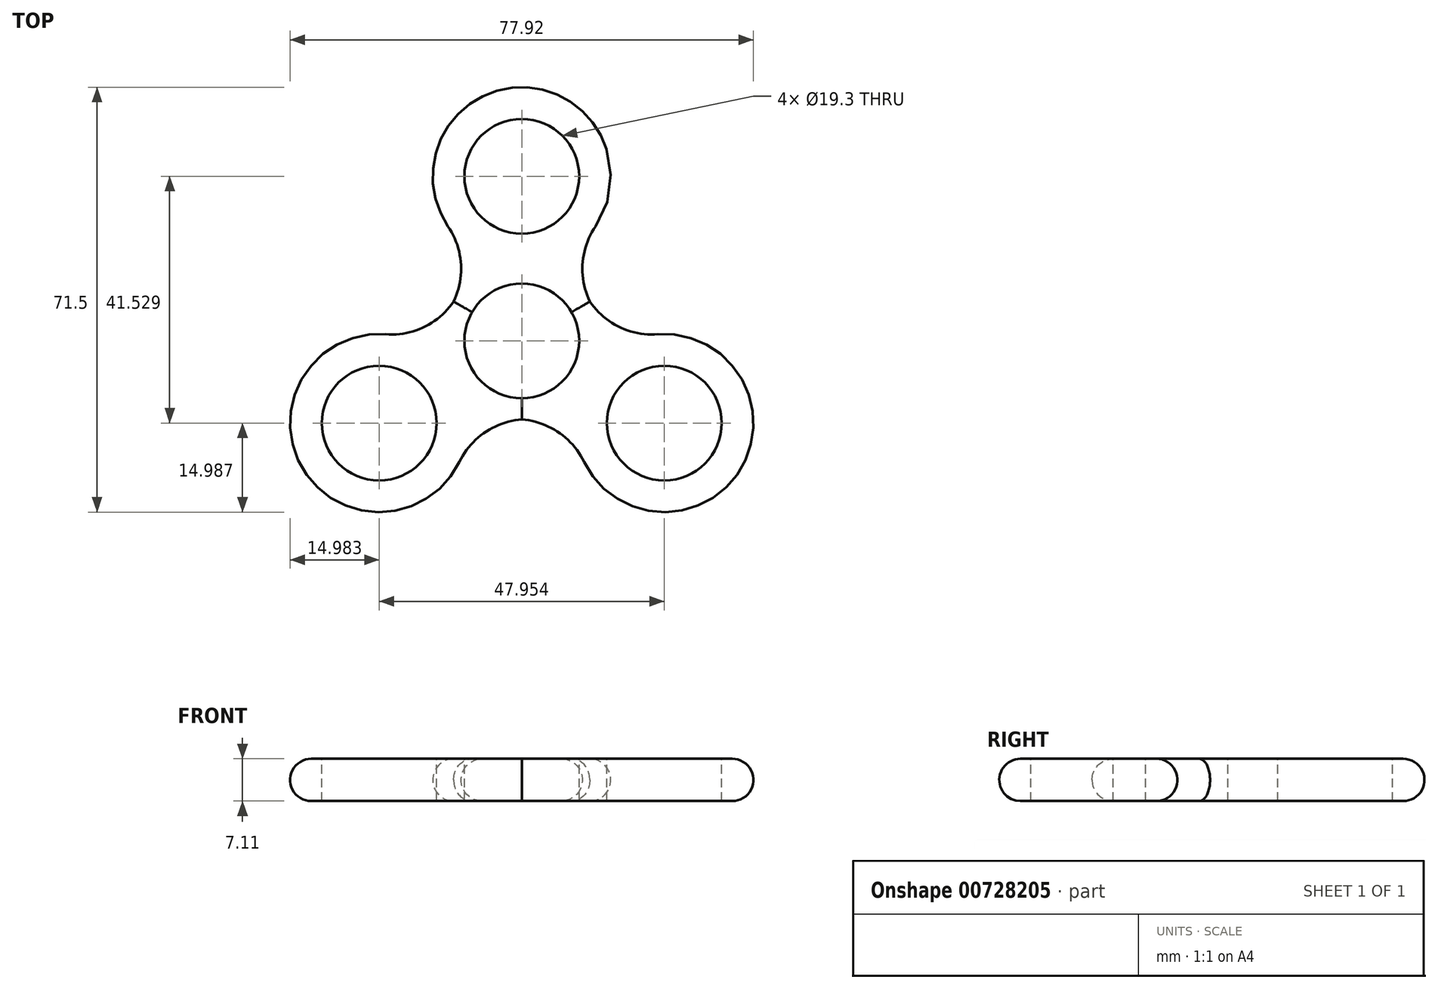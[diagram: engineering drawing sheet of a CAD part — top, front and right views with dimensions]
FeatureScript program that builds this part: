
annotation { "Feature Type Name" : "Feature", "Feature Type Description" : "" }
export const myFeature = defineFeature(function(context is Context, id is Id, definition is map)
    precondition{}
    {
        {
            var Q0;
            Q0=qCreatedBy(makeId("Top.planeOp"),FACE);
            var sketch = newSketch(context, id + "F0", { "sketchPlane" : qUnion([Q0])});
            skArc(sketch, "E0", {"start": v(12.4, 19.26) * mm, "mid": v(0, 42.67) * mm, "end": v(-12.4, 19.26) * mm});
            skArc(sketch, "E1.1.0", {"start": v(-22.88, 1.1) * mm, "mid": v(-36.96, -21.34) * mm, "end": v(-10.48, -20.36) * mm});
            skArc(sketch, "E1.2.0", {"start": v(10.48, -20.36) * mm, "mid": v(36.96, -21.34) * mm, "end": v(22.88, 1.1) * mm});
            skPoint(sketch, "E1.center", {"position": v(0, 0) * mm});
            skPoint(sketch, "E2.visualSharp", {"position": v(-12.53, -4.17) * mm});
            skArc(sketch, "E2.filletArc", {"start": v(-22.88, 1.1) * mm, "mid": v(-16.21, 2.44) * mm, "end": v(-11.19, 7.02) * mm});
            skPoint(sketch, "E3.visualSharp", {"position": v(12.53, -4.17) * mm});
            skArc(sketch, "E3.filletArc", {"start": v(11.19, 7.02) * mm, "mid": v(16.21, 2.44) * mm, "end": v(22.88, 1.1) * mm});
            skPoint(sketch, "E4.visualSharp", {"position": v(2.66, 12.94) * mm});
            skArc(sketch, "E4.filletArc", {"start": v(12.4, 19.26) * mm, "mid": v(10.22, 12.82) * mm, "end": v(11.67, 6.18) * mm});
            skPoint(sketch, "E5.visualSharp", {"position": v(-2.66, 12.94) * mm});
            skArc(sketch, "E5.filletArc", {"start": v(-11.67, 6.18) * mm, "mid": v(-10.22, 12.82) * mm, "end": v(-12.4, 19.26) * mm});
            skPoint(sketch, "E6.visualSharp", {"position": v(-9.88, -8.77) * mm});
            skArc(sketch, "E6.filletArc", {"start": v(0.48, -13.2) * mm, "mid": v(-6, -15.26) * mm, "end": v(-10.48, -20.36) * mm});
            skPoint(sketch, "E7.visualSharp", {"position": v(9.88, -8.77) * mm});
            skArc(sketch, "E7.filletArc", {"start": v(10.48, -20.36) * mm, "mid": v(6, -15.26) * mm, "end": v(-0.48, -13.2) * mm});
            skArc(sketch, "E8.trimOffspring", {"start": v(-11.19, 7.02) * mm, "mid": v(-11.44, 6.6) * mm, "end": v(-11.67, 6.18) * mm, "construction": true});
            skArc(sketch, "E9.trimOffspring", {"start": v(-0.48, -13.2) * mm, "mid": v(0, -13.2) * mm, "end": v(0.48, -13.2) * mm, "construction": true});
            skArc(sketch, "E10.trimOffspring", {"start": v(-11.19, 7.02) * mm, "mid": v(-11.44, 6.6) * mm, "end": v(-11.67, 6.18) * mm});
            skArc(sketch, "E11.trimOffspring", {"start": v(11.67, 6.18) * mm, "mid": v(11.44, 6.6) * mm, "end": v(11.19, 7.02) * mm});
            skArc(sketch, "E12.trimOffspring", {"start": v(-0.48, -13.2) * mm, "mid": v(0, -13.2) * mm, "end": v(0.48, -13.2) * mm});
            skSolve(sketch);
        }
        {
            var Q0;
            Q0 = qSketchRegion(id + "F0", true);
            extrude(context, id + "F1", {"entities" : qUnion([Q0]), "depth" : 7.11 * mm, "offsetDistance" : 25.4 * mm});
        }
        {
            var Q0;
            Q0=makeQuery(id+"F1.opExtrude","CAP_FACE",FACE,{"disambiguationData":[OSD([sQuery(id+"F0.wireOp",EDGE,"E0"),sQuery(id+"F0.wireOp",EDGE,"60gk7Q8c-7hSc-AToD-YciR-2eRYY725DYxX"),sQuery(id+"F0.wireOp",EDGE,"3hoOJwKx-Mt2q-Xiem-dPVq-RfPuo6QVFx0r"),sQuery(id+"F0.wireOp",EDGE,"E1.1.0"),sQuery(id+"F0.wireOp",EDGE,"E1.1.1"),sQuery(id+"F0.wireOp",EDGE,"E1.2.0"),sQuery(id+"F0.wireOp",EDGE,"E1.2.1"),sQuery(id+"F0.wireOp",EDGE,"E2.filletArc"),sQuery(id+"F0.wireOp",EDGE,"E3.filletArc"),sQuery(id+"F0.wireOp",EDGE,"E4.filletArc"),sQuery(id+"F0.wireOp",EDGE,"E5.filletArc"),sQuery(id+"F0.wireOp",EDGE,"E6.filletArc"),sQuery(id+"F0.wireOp",EDGE,"E7.filletArc")])],"isStart":false});
            var Q1;
            Q1=makeQuery(id+"F1.opExtrude","CAP_FACE",FACE,{"disambiguationData":[OSD([sQuery(id+"F0.wireOp",EDGE,"E0"),sQuery(id+"F0.wireOp",EDGE,"60gk7Q8c-7hSc-AToD-YciR-2eRYY725DYxX"),sQuery(id+"F0.wireOp",EDGE,"3hoOJwKx-Mt2q-Xiem-dPVq-RfPuo6QVFx0r"),sQuery(id+"F0.wireOp",EDGE,"E1.1.0"),sQuery(id+"F0.wireOp",EDGE,"E1.1.1"),sQuery(id+"F0.wireOp",EDGE,"E1.2.0"),sQuery(id+"F0.wireOp",EDGE,"E1.2.1"),sQuery(id+"F0.wireOp",EDGE,"E2.filletArc"),sQuery(id+"F0.wireOp",EDGE,"E3.filletArc"),sQuery(id+"F0.wireOp",EDGE,"E4.filletArc"),sQuery(id+"F0.wireOp",EDGE,"E5.filletArc"),sQuery(id+"F0.wireOp",EDGE,"E6.filletArc"),sQuery(id+"F0.wireOp",EDGE,"E7.filletArc")])],"isStart":true});
            fillet(context, id + "F2", {"entities" : qUnion([Q0, Q1]), "radius" : 3.56 * mm, "tangentPropagation" : true, "allowEdgeOverflow" : false});
        }
        {
            var Q0;
            Q0=makeQuery(id+"F1.opExtrude","CAP_FACE",FACE,{"disambiguationData":[OSD([sQuery(id+"F0.wireOp",EDGE,"E0"),sQuery(id+"F0.wireOp",EDGE,"E1.1.0"),sQuery(id+"F0.wireOp",EDGE,"E1.2.0"),sQuery(id+"F0.wireOp",EDGE,"E2.filletArc"),sQuery(id+"F0.wireOp",EDGE,"E3.filletArc"),sQuery(id+"F0.wireOp",EDGE,"E4.filletArc"),sQuery(id+"F0.wireOp",EDGE,"E5.filletArc"),sQuery(id+"F0.wireOp",EDGE,"E6.filletArc"),sQuery(id+"F0.wireOp",EDGE,"E7.filletArc")])],"isStart":false});
            var sketch = newSketch(context, id + "F3", { "sketchPlane" : qUnion([Q0])});
            skCircle(sketch, "E13", {"center": v(0, 0) * mm, "radius": 9.65 * mm});
            skCircle(sketch, "E14", {"center": v(0, 27.69) * mm, "radius": 9.65 * mm});
            skCircle(sketch, "E15.1.0", {"center": v(-23.98, -13.84) * mm, "radius": 9.65 * mm});
            skCircle(sketch, "E15.2.0", {"center": v(23.98, -13.84) * mm, "radius": 9.65 * mm});
            skSolve(sketch);
        }
        {
            var Q0;
            Q0 = qSketchRegion(id + "F3", true);
            extrude(context, id + "F4", {"entities" : qUnion([Q0]), "operationType" : NewBodyOperationType.REMOVE, "endBound" : BoundingType.THROUGH_ALL, "oppositeDirection" : true, "depth" : 25.4 * mm, "offsetDistance" : 25.4 * mm});
        }
    });
